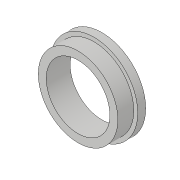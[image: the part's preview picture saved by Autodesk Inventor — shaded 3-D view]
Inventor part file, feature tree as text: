
AUTODESK INVENTOR PART (.ipt)
format: ipt  version: 2018.3 (Build 223284000, 284)  size: 100,864 bytes
history: native  units: in
note: dims shown in document units (in); Inventor stores cm internally (conversion verified against a paired STEP export)
features: extrude x3, sketch x3
ambient origin geometry x8: Origin, YZ Plane, XZ Plane, XY Plane, X Axis, Y Axis, Z Axis, Center Point
bodies: Solid1 (feature_tree)
feature tree (6):
  extrude  "Extrusion1"  Depth=0.6875in
  extrude  "Extrusion2"  Depth=0.0625in TaperAngle=0.0deg
  extrude  "Extrusion3"  Depth=0.125in TaperAngle=0.0deg
  sketch  "Sketch1"  dims[d0=0.5in d3=0.6875in]
  sketch  "Sketch2"  dims[d4=0.0312in d5=0.0625in d6=0.0in]
  sketch  "Sketch3"  dims[d7=0.5in d8=0.6875in d9=0.0312in d10=0.125in d11=0.0in d12=0.125in d13=0.0in]
